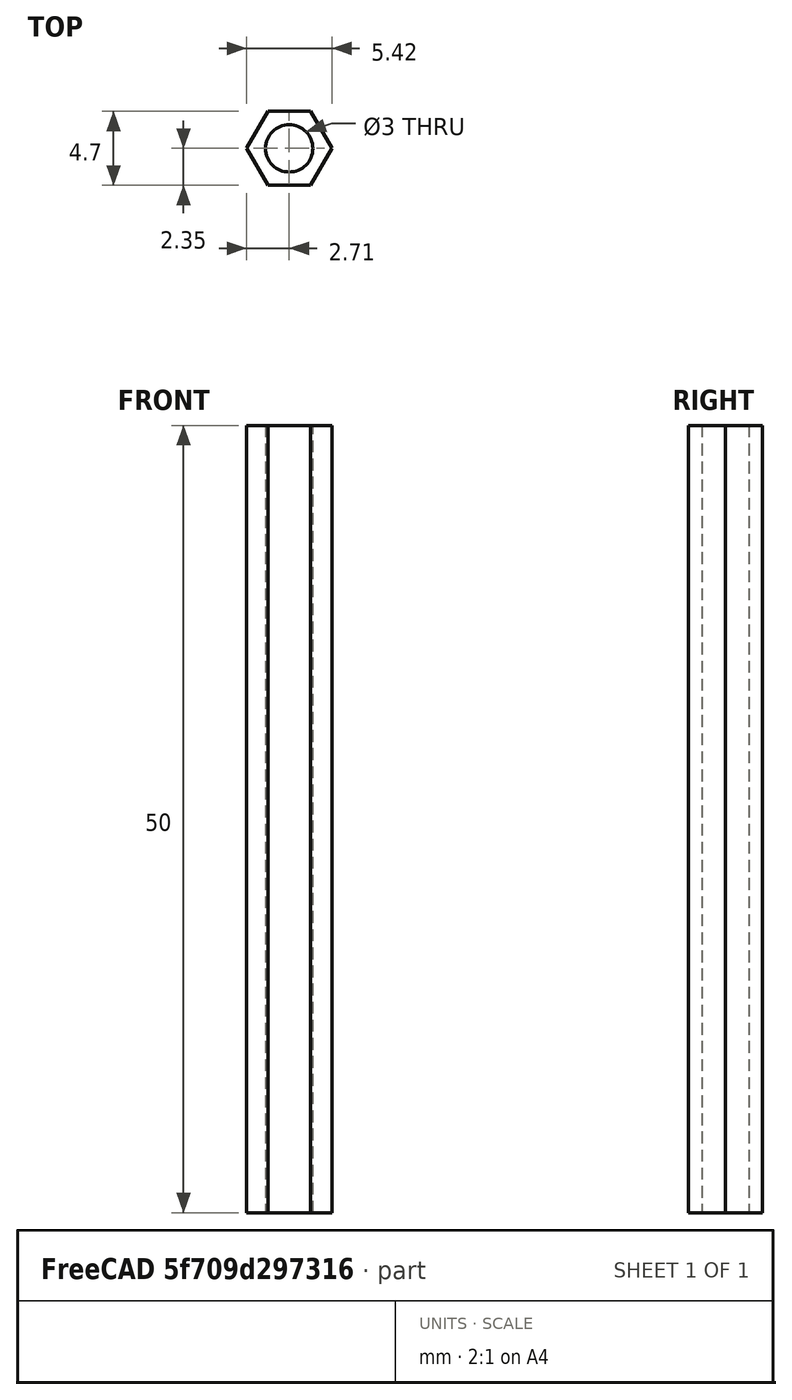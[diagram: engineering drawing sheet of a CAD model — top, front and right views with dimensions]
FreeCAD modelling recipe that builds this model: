
FCSTD DOCUMENT  (FreeCAD 0.18.4R)
Label: coxial_M3_50mm
License: All rights reserved
LicenseURL: http://en.wikipedia.org/wiki/All_rights_reserved
objects: Sketcher::SketchObject×1, PartDesign::Pad×1, PartDesign::Body×1
note: 4 computed .brp shape members not serialized (recipe doc carries the construction recipe); baked Part::Feature solids carry a one-line shape summary decoded from their .brp

FEATURE [Sketcher::SketchObject] Sketch
  MapMode = 5
  Support = -> [XY_Plane001]
  sketch-geometry (8):
    g0: Circle CenterX=0 CenterY=0 CenterZ=0 NormalX=0 NormalY=0 NormalZ=1 AngleXU=0 Radius=1.5
    g1: LineSegment StartX=1.35677 StartY=-2.35 StartZ=0 EndX=2.71355 EndY=-4e-16 EndZ=0
    g2: LineSegment StartX=2.71355 StartY=-4e-16 StartZ=0 EndX=1.35677 EndY=2.35 EndZ=0
    g3: LineSegment StartX=1.35677 StartY=2.35 StartZ=0 EndX=-1.35677 EndY=2.35 EndZ=0
    g4: LineSegment StartX=-1.35677 StartY=2.35 StartZ=0 EndX=-2.71355 EndY=1.8e-15 EndZ=0
    g5: LineSegment StartX=-2.71355 StartY=1.9e-15 StartZ=0 EndX=-1.35677 EndY=-2.35 EndZ=0
    g6: LineSegment StartX=-1.35677 StartY=-2.35 StartZ=0 EndX=1.35677 EndY=-2.35 EndZ=0
    g7: Circle [constr] CenterX=0 CenterY=0 CenterZ=0 NormalX=0 NormalY=0 NormalZ=1 AngleXU=0 Radius=2.71355
  constraints (18):
    c: Radius(g0) = 1.5
    c: Coincident(g0,g-1)
    c: Coincident(g1,g2)
    c: Coincident(g2,g3)
    c: Coincident(g3,g4)
    c: Coincident(g4,g5)
    c: Coincident(g5,g6)
    c: Coincident(g6,g1)
    c: Equal(g1, g2-g6) x5
    c: PointOnObject(g1,g7)
    c: PointOnObject(g2,g7)
    c: PointOnObject(g3,g7)
    c: PointOnObject(g4,g7)
    c: PointOnObject(g5,g7)
    c: PointOnObject(g6,g7)
    c: Distance(g2,g4) = 4.7
    c: Coincident(g7,g0)
    c: Horizontal(g3)
FEATURE [PartDesign::Pad] Pad
  Length = 50
  Length2 = 100
  Profile = -> Sketch
  Type = 0
FEATURE [PartDesign::Body] Body
  Group = -> [Sketch,Pad]
  Origin = -> Origin001
  Tip = -> Pad
